# Revit family: Reece_Sink_Shaws_Lancaster_Butler Sink_Double Bowl
name_source: partatom
category: Plumbing Fixtures
revit_build: Autodesk Revit 2018 (Build: 20190510_1515(x64)
units: mm (PartAtom-declared; Revit-internal decimal feet)

## family parameters
Cut with Voids When Loaded = No
Host = Face
Part Type = Normal
Room Calculation Point = Yes
Round Connector Dimension = Use Diameter
Shared = Yes

## types (1)
- 795 mm_46 L_White
    CWFU = 0
    Default Elevation = 1000 mm  [stored 3.28084 ft]
    Description = Shaws Lancaster Double Bowl 800mm Fireclay Butler Sink
    Disclaimer = THIS FILE IS THE PROPERTY OF THE REECE GROUP. IT MAY NOT BE REPRODUCED, REVERSE-ENGINEERED OR MODIFIED. ANY REPUBLICATION, TRANSMISSION OR DISTRIBUTION FOR THE PURPOSE OF COMMERCIALLY EXPLOITING THE FILES IS PROHIBITED.
    HWFU = 0
    Keynote = Product #2029372, Reece_Sink_Shaws_Lancaster_Butler Sink_Double Bowl - 795 mm_46 L_White
    Manufacturer = Shaws
    Model = Lancaster
    Reece_Detail_Bowl Type = Double Bowl
    Reece_Detail_Disclaimer = THIS FILE IS THE PROPERTY OF THE REECE GROUP. IT MAY NOT BE REPRODUCED, REVERSE-ENGINEERED OR MODIFIED. ANY REPUBLICATION, TRANSMISSION OR DISTRIBUTION FOR THE PURPOSE OF COMMERCIALLY EXPLOITING THE FILES IS PROHIBITED.
    Reece_Detail_Installation = Butler Sink
    Reece_Detail_Shape = No Drainer
    Reece_Detail_Taphole Configuration = No Taphole
    Reece_Material_Main = Reece_Ceramic_Fine Fire Clay_White
    Reece_Material_Secondary = Reece_Metal_Stainless Steel_Satin
    Reece_Overall_Capacity = 46 L
    Reece_Overall_Depth = 465 mm  [stored 1.52559 ft]
    Reece_Overall_Height = 229 mm
    Reece_Overall_Width = 777 mm
    Reece_Product_Brand = Shaws
    Reece_Product_Description = Shaws Lancaster Double Bowl 800mm Fireclay Butler Sink
    Reece_Product_Mount = Butler Style
    Reece_Product_Number = 2029372
    Reece_Product_Sub Brand = Lancaster
    Reece_Product_Type = Sink
    Reece_Product_Web Page = https://www.reece.com.au
    Reece_Sink_Outlet = 40 mm  [stored 0.131234 ft]
    Type Comments = Sink
    URL = https://www.reece.com.au
    WFU = 0

note: [stored X ft] marks values corroborated as IEEE doubles in the binary element streams (Revit-internal decimal feet)

## geometry (parser evidence)
native form markers: Sweep x5
no freeform markers — native parametric forms only
